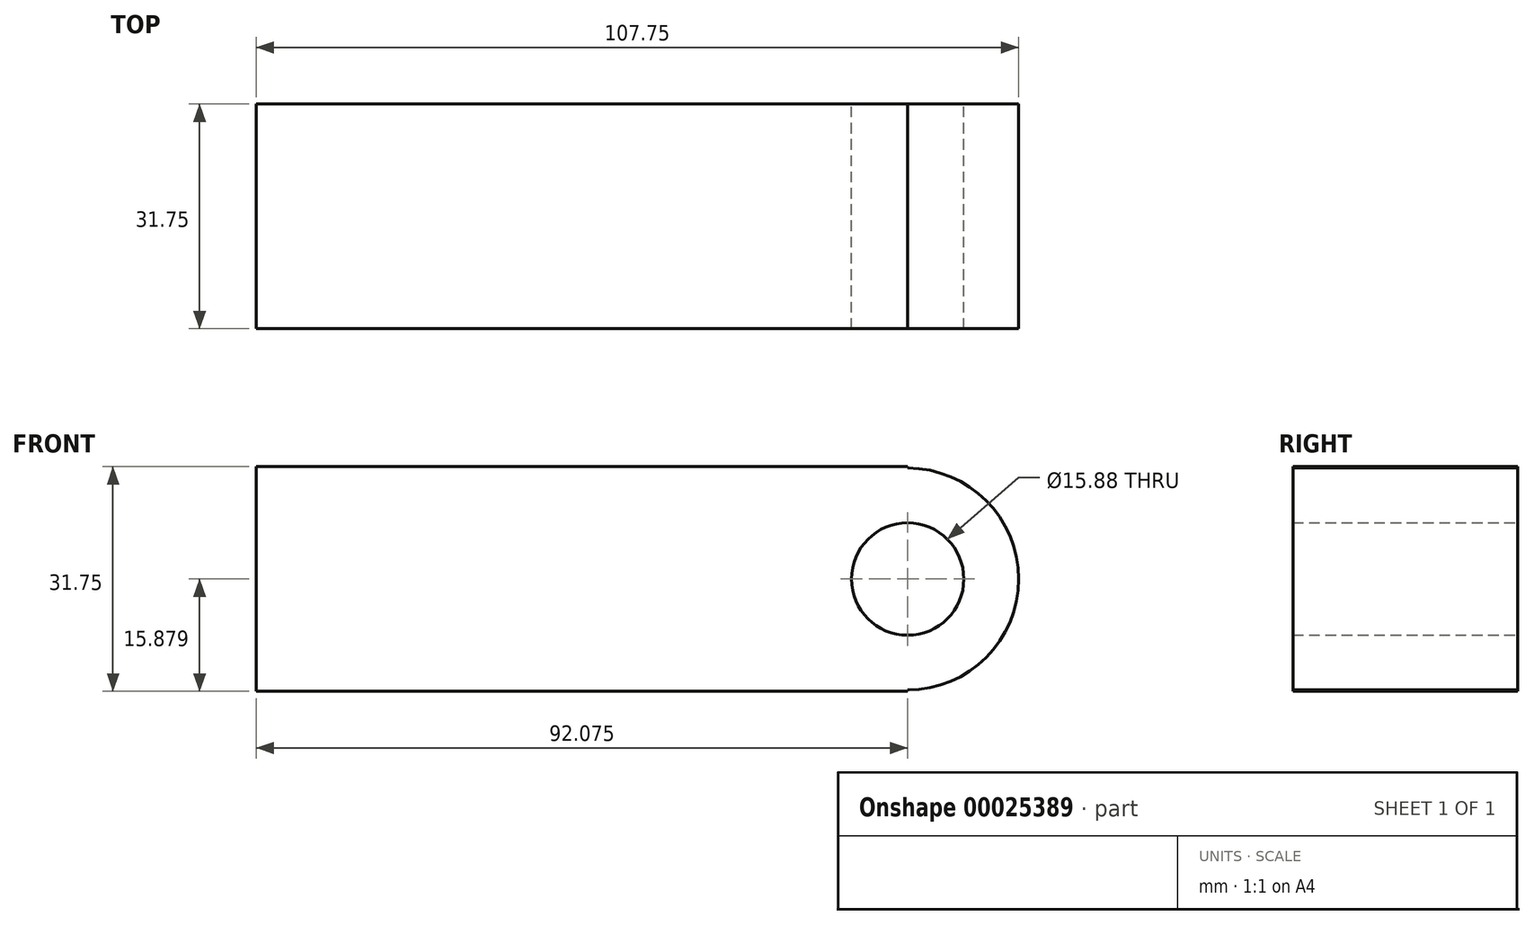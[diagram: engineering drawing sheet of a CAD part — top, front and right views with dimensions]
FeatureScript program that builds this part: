
annotation { "Feature Type Name" : "Feature", "Feature Type Description" : "" }
export const myFeature = defineFeature(function(context is Context, id is Id, definition is map)
    precondition{}
    {
        {
            var Q0;
            Q0=qCreatedBy(makeId("Front.planeOp"),FACE);
            var sketch = newSketch(context, id + "F0", { "sketchPlane" : qUnion([Q0])});
            skLineSegment(sketch, "E0.bottom", {"start": v(-60.05, 14.33) * mm, "end": v(32.02, 14.33) * mm});
            skLineSegment(sketch, "E0.top", {"start": v(-60.05, -17.42) * mm, "end": v(32.02, -17.42) * mm});
            skLineSegment(sketch, "E0.left", {"start": v(-60.05, 14.33) * mm, "end": v(-60.05, -17.42) * mm});
            skLineSegment(sketch, "E1.0", {"start": v(-44.18, 14.33) * mm, "end": v(-44.18, -17.42) * mm});
            skLineSegment(sketch, "E2.0", {"start": v(32.02, 14.33) * mm, "end": v(32.02, -17.42) * mm});
            skCircle(sketch, "E3", {"center": v(32.02, -1.54) * mm, "radius": 7.94 * mm});
            skCircle(sketch, "E4", {"center": v(32.02, -1.54) * mm, "radius": 15.68 * mm});
            skSolve(sketch);
        }
        {
            var Q0;
            Q0 = qSketchRegion(id + "F0", true);
            extrude(context, id + "F1", {"entities" : qUnion([Q0]), "depth" : 31.75 * mm});
        }
    });
